# Revit family: Damper_Volume_Control-Carnes-Alum-FDHB
name_source: partatom
category: Duct Accessories
revit_build: Autodesk Revit MEP 2012 (Build: 20110309_2315(x64)
units: mm (PartAtom-declared; Revit-internal decimal feet)

## types (1)
- FDHB
    04 CSI = 08 91 00
    95 CSI = 10200
    Actual Height = 24"
    Actual Width = 24"
    Assembly Code = B2010300
    Blade Material = Metal - Carnes - Steel - Galvanized
    Blades Length = 22 1/2"
    Catalog URL = http://www.carnes.com
    Default Elevation = 0"
    Depth = 4 1/2"
    Description = Low Leakage Volume Control Dampers
    Duct Connector 1 = Duct Connection 1
    Duct Connector 2 = Duct Connection 2
    Frame Material = Metal - Carnes - Steel - Galvanized
    Free Area Note = See Spec Sheet URL
    Height = 24"
    Installation and Maintenance URL = http://www.carnes.com
    Manufacturer = CARNES COMPANY
    Manufacturer Fax = 608-845-6470
    Maximum Horinzontal Size = 52"W x 72" (Single Section), Multi-section unlimited
    Maximum Size Note = Over 36” wide or 48” high, blade linkage will be modified.
    Maximum System Pressure = 1.00 in-wg
    Maximum System Velocity = 2600 FPM
    Maximum Vertical Size = 52"W x 72" (Single Section), Multi-section unlimited
    Minimum Size = 5"W x 4"H
    Model = FDHB
    Offset = 1"
    Product Line = Low Leakage Volume Control Dampers
    Product Page URL = http://www.carnes.com
    Spec Sheet URL = http://www.carnes.com
    Subcategory = Louvers and Dampers
    URL = http://www.carnes.com
    Warranty URL = http://www.carnes.com
    Width = 24"
    ecoScorecard Product Page = http://ecoscorecard.com

## geometry (parser evidence)
native form markers: Blend x4, Sweep x5
no freeform markers — native parametric forms only
